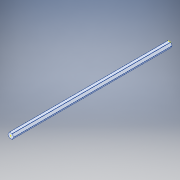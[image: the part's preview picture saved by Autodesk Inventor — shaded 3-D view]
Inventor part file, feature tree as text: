
AUTODESK INVENTOR PART (.ipt)
format: ipt  version: 2017 (Build 210142000, 142)  size: 151,552 bytes
history: native  units: in
note: dims shown in document units (in); Inventor stores cm internally (conversion verified against a paired STEP export)
features: sketch x7, split x1, fillet x1
ambient origin geometry x8: Origin, YZ Plane, XZ Plane, XY Plane, X Axis, Y Axis, Z Axis, Center Point
bodies: Solid1 (feature_tree)
feature tree (9):
  sketch  "Sketch1"  dims[d11=16.0in]
  split  "Split1"
  sketch  "Sketch3"  dims[d13=7.8125in]
  sketch  "Sketch4"  dims[d14=3.5453in]
  sketch  "Sketch5"  dims[d15=3.5453in]
  sketch  "Sketch6"
  sketch  "Sketch7"
  sketch  "Sketch2"  dims[d12=7.8125in]
  fillet  "Fillet1"  Radius=8.5in
